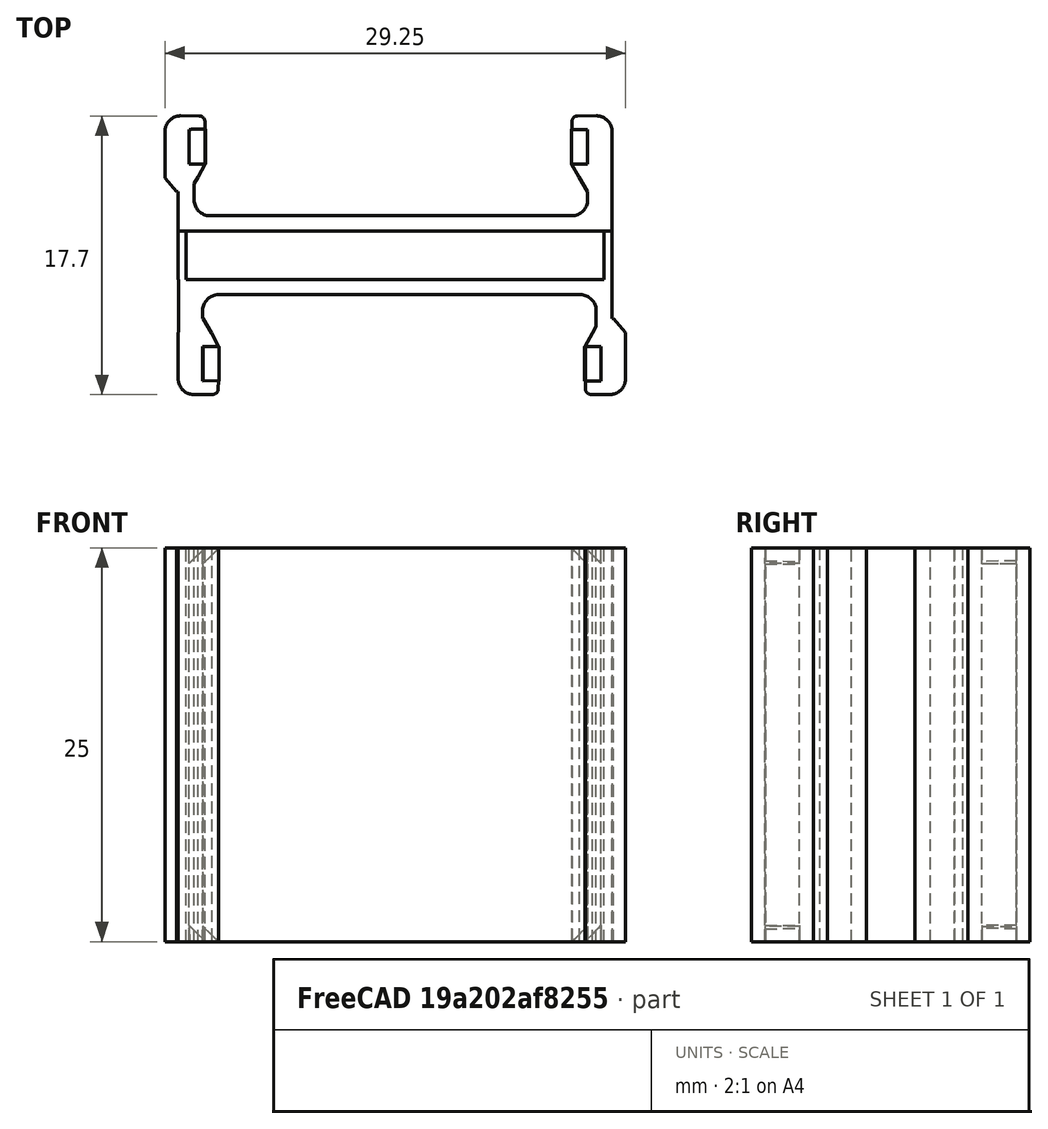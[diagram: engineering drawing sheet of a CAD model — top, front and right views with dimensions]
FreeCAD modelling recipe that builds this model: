
FCSTD DOCUMENT  (FreeCAD 0.18.4R)
Label: GSMBoardClip3
License: All rights reserved
LicenseURL: http://en.wikipedia.org/wiki/All_rights_reserved
objects: Sketcher::SketchObject×14, PartDesign::Pad×14, Part::MultiFuse×7, Part::Fillet×6, Part::Box×2, Mesh::Feature×1
note: 57 computed .brp shape members not serialized (recipe doc carries the construction recipe); baked Part::Feature solids carry a one-line shape summary decoded from their .brp

FEATURE [Sketcher::SketchObject] Sketch
  MapMode = 5
  sketch-geometry (8):
    g0: LineSegment StartX=-13.9908 StartY=-4.48975 StartZ=0 EndX=10.9903 EndY=-4.48975 EndZ=0
    g1: LineSegment StartX=12.5295 StartY=-5.45766 StartZ=0 EndX=-15.0007 EndY=-5.45766 EndZ=0
    g2: LineSegment StartX=-15.0007 StartY=-1.98555 StartZ=0 EndX=-13.9908 EndY=-1.98555 EndZ=0
    g3: LineSegment StartX=-13.9908 StartY=-1.98555 StartZ=0 EndX=-13.9908 EndY=-4.48975 EndZ=0
    g4: LineSegment StartX=-15.0007 StartY=-5.45766 StartZ=0 EndX=-15.0007 EndY=-1.98555 EndZ=0
    g5: LineSegment StartX=10.9903 StartY=-4.48975 StartZ=0 EndX=11.0098 EndY=-1.99154 EndZ=0
    g6: LineSegment StartX=11.0098 StartY=-1.99154 StartZ=0 EndX=12.5373 EndY=-1.98538 EndZ=0
    g7: LineSegment StartX=12.5373 StartY=-1.98538 StartZ=0 EndX=12.5295 EndY=-5.45766 EndZ=0
  constraints (13):
    c: Horizontal(g0)
    c: Horizontal(g1)
    c: Coincident(g2,g3)
    c: Coincident(g4,g2)
    c: Horizontal(g2)
    c: Vertical(g3)
    c: Vertical(g4)
    c: Coincident(g0,g3)
    c: Coincident(g4,g1)
    c: Coincident(g1,g7)
    c: Coincident(g0,g5)
    c: Coincident(g5,g6)
    c: Coincident(g6,g7)
FEATURE [Sketcher::SketchObject] Sketch004
  MapMode = 5
  Placement = pos=(-7.3,1,6.03) rot=(1,0,0;1.5708rad)
  sketch-geometry (3):
    g0: LineSegment StartX=-7.00166 StartY=-5.01077 StartZ=0 EndX=-6.98953 EndY=-6.02972 EndZ=0
    g1: LineSegment StartX=-6.98953 StartY=-6.02972 StartZ=0 EndX=-5.96627 EndY=-6.02972 EndZ=0
    g2: LineSegment StartX=-7.00166 StartY=-5.01077 StartZ=0 EndX=-5.96627 EndY=-6.02972 EndZ=0
  constraints (3):
    c: Coincident(g0,g1)
    c: Coincident(g2,g0)
    c: Coincident(g2,g1)
FEATURE [PartDesign::Pad] Pad004  label="stopper002"
  Length = 2.2
  Length2 = 100
  Placement = pos=(-7.3,1,6.03) rot=(1,0,0;1.5708rad)
  Profile = -> Sketch004
  Type = 0
FEATURE [Sketcher::SketchObject] Sketch008
  MapMode = 5
  Placement = pos=(-13.3,1,24.03) rot=(1,0,0;1.5708rad)
  sketch-geometry (3):
    g0: LineSegment StartX=-0.005347 StartY=0.971544 StartZ=0 EndX=-1.00207 EndY=-0.002707 EndZ=0
    g1: LineSegment StartX=-1.00207 StartY=-0.002707 StartZ=0 EndX=-1.00779 EndY=0.969763 EndZ=0
    g2: LineSegment StartX=-1.00779 StartY=0.969763 StartZ=0 EndX=-0.005347 EndY=0.971544 EndZ=0
  constraints (3):
    c: Coincident(g0,g1)
    c: Coincident(g1,g2)
    c: Coincident(g2,g0)
FEATURE [PartDesign::Pad] Pad008  label="stopper001"
  Length = 2.2
  Length2 = 100
  Placement = pos=(-13.3,1,24.03) rot=(1,0,0;1.5708rad)
  Profile = -> Sketch008
  Type = 0
FEATURE [Sketcher::SketchObject] Sketch009
  MapMode = 5
  Placement = pos=(-5.3,1,0) rot=(0,0,1;0rad)
  sketch-geometry (11):
    g0: LineSegment StartX=-10.5532 StartY=0.855362 StartZ=0 EndX=-8.36858 EndY=0.849458 EndZ=0
    g1: LineSegment StartX=-8.00975 StartY=0.49381 StartZ=0 EndX=-8.00369 EndY=-0.0300228 EndZ=0
    g2: LineSegment StartX=-8.00369 StartY=-0.0300228 StartZ=0 EndX=-8.99915 EndY=-0.016209 EndZ=0
    g3: LineSegment StartX=-8.99915 StartY=-0.016209 StartZ=0 EndX=-8.99963 EndY=-2.20954 EndZ=0
    g4: LineSegment StartX=-8.99963 StartY=-2.20954 StartZ=0 EndX=-7.98693 EndY=-2.20954 EndZ=0
    g5: LineSegment StartX=-7.98693 StartY=-2.20954 StartZ=0 EndX=-8.44936 EndY=-3.04943 EndZ=0
    g6: LineSegment StartX=-8.44936 StartY=-3.04943 StartZ=0 EndX=-8.98872 EndY=-3.96758 EndZ=0
    g7: LineSegment StartX=-8.98872 StartY=-3.96758 StartZ=0 EndX=-9.79483 EndY=-3.96363 EndZ=0
    g8: LineSegment StartX=-9.79483 StartY=-3.96363 StartZ=0 EndX=-10.5532 EndY=-3.09064 EndZ=0
    g9: LineSegment StartX=-10.5532 StartY=-3.09064 StartZ=0 EndX=-10.5532 EndY=0.855362 EndZ=0
    g10: ArcOfCircle CenterX=-8.36955 CenterY=0.489641 CenterZ=0 NormalX=0 NormalY=0 NormalZ=1 AngleXU=0 Radius=0.359818 StartAngle=0.0115851 EndAngle=1.56809
  constraints (11):
    c: Coincident(g1,g2)
    c: Coincident(g2,g3)
    c: Coincident(g3,g4)
    c: Coincident(g4,g5)
    c: Coincident(g5,g6)
    c: Coincident(g6,g7)
    c: Tangent(g0,g10) = 1.5708
    c: Tangent(g1,g10) = 1.5708
    c: Coincident(g9,g0)
    c: Coincident(g9,g8)
    c: Coincident(g8,g7)
FEATURE [PartDesign::Pad] Pad009  label="Snap001"
  Length = 25
  Length2 = 100
  Placement = pos=(-5.3,1,0) rot=(0,0,1;0rad)
  Profile = -> Sketch009
  Type = 0
FEATURE [Part::MultiFuse] Fusion  label="SnapLeft"
  Shapes = -> [Pad009,Pad008,Pad004]
FEATURE [Sketcher::SketchObject] Sketch010
  MapMode = 5
  Placement = pos=(-7.3,1,6.03) rot=(1,0,0;1.5708rad)
  sketch-geometry (3):
    g0: LineSegment StartX=-7.00166 StartY=-5.01077 StartZ=0 EndX=-6.98953 EndY=-6.02972 EndZ=0
    g1: LineSegment StartX=-6.98953 StartY=-6.02972 StartZ=0 EndX=-5.96627 EndY=-6.02972 EndZ=0
    g2: LineSegment StartX=-7.00166 StartY=-5.01077 StartZ=0 EndX=-5.96627 EndY=-6.02972 EndZ=0
  constraints (3):
    c: Coincident(g0,g1)
    c: Coincident(g2,g0)
    c: Coincident(g2,g1)
FEATURE [PartDesign::Pad] Pad010  label="stopper003"
  Length = 2.2
  Length2 = 100
  Placement = pos=(-7.3,1,6.03) rot=(1,0,0;1.5708rad)
  Profile = -> Sketch010
  Type = 0
FEATURE [Sketcher::SketchObject] Sketch011
  MapMode = 5
  Placement = pos=(-13.3,1,24.03) rot=(1,0,0;1.5708rad)
  sketch-geometry (3):
    g0: LineSegment StartX=-0.005347 StartY=0.971544 StartZ=0 EndX=-1.00207 EndY=-0.002707 EndZ=0
    g1: LineSegment StartX=-1.00207 StartY=-0.002707 StartZ=0 EndX=-1.00779 EndY=0.969763 EndZ=0
    g2: LineSegment StartX=-1.00779 StartY=0.969763 StartZ=0 EndX=-0.005347 EndY=0.971544 EndZ=0
  constraints (3):
    c: Coincident(g0,g1)
    c: Coincident(g1,g2)
    c: Coincident(g2,g0)
FEATURE [PartDesign::Pad] Pad011  label="stopper004"
  Length = 2.2
  Length2 = 100
  Placement = pos=(-13.3,1,24.03) rot=(1,0,0;1.5708rad)
  Profile = -> Sketch011
  Type = 0
FEATURE [Sketcher::SketchObject] Sketch012
  MapMode = 5
  Placement = pos=(-5.3,1,0) rot=(0,0,1;0rad)
  sketch-geometry (11):
    g0: LineSegment StartX=-10.5532 StartY=0.855362 StartZ=0 EndX=-8.36858 EndY=0.849458 EndZ=0
    g1: LineSegment StartX=-8.00975 StartY=0.49381 StartZ=0 EndX=-8.00369 EndY=-0.0300228 EndZ=0
    g2: LineSegment StartX=-8.00369 StartY=-0.0300228 StartZ=0 EndX=-8.99915 EndY=-0.016209 EndZ=0
    g3: LineSegment StartX=-8.99915 StartY=-0.016209 StartZ=0 EndX=-8.99963 EndY=-2.20954 EndZ=0
    g4: LineSegment StartX=-8.99963 StartY=-2.20954 StartZ=0 EndX=-7.98693 EndY=-2.20954 EndZ=0
    g5: LineSegment StartX=-7.98693 StartY=-2.20954 StartZ=0 EndX=-8.44936 EndY=-3.04943 EndZ=0
    g6: LineSegment StartX=-8.44936 StartY=-3.04943 StartZ=0 EndX=-8.98872 EndY=-3.96758 EndZ=0
    g7: LineSegment StartX=-8.98872 StartY=-3.96758 StartZ=0 EndX=-9.79483 EndY=-3.96363 EndZ=0
    g8: LineSegment StartX=-9.79483 StartY=-3.96363 StartZ=0 EndX=-10.5532 EndY=-3.09064 EndZ=0
    g9: LineSegment StartX=-10.5532 StartY=-3.09064 StartZ=0 EndX=-10.5532 EndY=0.855362 EndZ=0
    g10: ArcOfCircle CenterX=-8.36955 CenterY=0.489641 CenterZ=0 NormalX=0 NormalY=0 NormalZ=1 AngleXU=0 Radius=0.359818 StartAngle=0.0115851 EndAngle=1.56809
  constraints (11):
    c: Coincident(g1,g2)
    c: Coincident(g2,g3)
    c: Coincident(g3,g4)
    c: Coincident(g4,g5)
    c: Coincident(g5,g6)
    c: Coincident(g6,g7)
    c: Tangent(g0,g10) = 1.5708
    c: Tangent(g1,g10) = 1.5708
    c: Coincident(g9,g0)
    c: Coincident(g9,g8)
    c: Coincident(g8,g7)
FEATURE [PartDesign::Pad] Pad012  label="Snap002"
  Length = 25
  Length2 = 100
  Placement = pos=(-5.3,1,0) rot=(0,0,1;0rad)
  Profile = -> Sketch012
  Type = 0
FEATURE [Part::MultiFuse] Fusion001  label="SnapRight"
  Placement = pos=(-3.3,0,25) rot=(0,1,0;3.14159rad)
  Shapes = -> [Pad012,Pad011,Pad010]
FEATURE [PartDesign::Pad] Pad
  Length = 25
  Length2 = 100
  Profile = -> Sketch
  Type = 0
FEATURE [Part::Fillet] Fillet
  Base = -> Pad
  Edges = 2 edges r=1: [Edge1,Edge2]
FEATURE [Part::Fillet] Fillet001
  Base = -> Fusion
  Edges = 1 edges r=1: [Edge59]
FEATURE [Part::Fillet] Fillet002
  Base = -> Fusion001
  Edges = 1 edges r=1: [Edge59]
FEATURE [Part::MultiFuse] Fusion002  label="GSMClip3_001"
  Shapes = -> [Fillet,Fillet001,Fillet002]
FEATURE [Sketcher::SketchObject] Sketch013
  MapMode = 5
  sketch-geometry (8):
    g0: LineSegment StartX=-13.9908 StartY=-4.48975 StartZ=0 EndX=10.9903 EndY=-4.48975 EndZ=0
    g1: LineSegment StartX=12.5295 StartY=-5.45766 StartZ=0 EndX=-15.0007 EndY=-5.45766 EndZ=0
    g2: LineSegment StartX=-15.0007 StartY=-1.98555 StartZ=0 EndX=-13.9908 EndY=-1.98555 EndZ=0
    g3: LineSegment StartX=-13.9908 StartY=-1.98555 StartZ=0 EndX=-13.9908 EndY=-4.48975 EndZ=0
    g4: LineSegment StartX=-15.0007 StartY=-5.45766 StartZ=0 EndX=-15.0007 EndY=-1.98555 EndZ=0
    g5: LineSegment StartX=10.9903 StartY=-4.48975 StartZ=0 EndX=11.0098 EndY=-1.99154 EndZ=0
    g6: LineSegment StartX=11.0098 StartY=-1.99154 StartZ=0 EndX=12.5373 EndY=-1.98538 EndZ=0
    g7: LineSegment StartX=12.5373 StartY=-1.98538 StartZ=0 EndX=12.5295 EndY=-5.45766 EndZ=0
  constraints (13):
    c: Horizontal(g0)
    c: Horizontal(g1)
    c: Coincident(g2,g3)
    c: Coincident(g4,g2)
    c: Horizontal(g2)
    c: Vertical(g3)
    c: Vertical(g4)
    c: Coincident(g0,g3)
    c: Coincident(g4,g1)
    c: Coincident(g1,g7)
    c: Coincident(g0,g5)
    c: Coincident(g5,g6)
    c: Coincident(g6,g7)
FEATURE [PartDesign::Pad] Pad013
  Length = 25
  Length2 = 100
  Profile = -> Sketch013
  Type = 0
FEATURE [Part::Fillet] Fillet003
  Base = -> Pad013
  Edges = 2 edges r=1: [Edge1,Edge2]
FEATURE [Sketcher::SketchObject] Sketch014
  MapMode = 5
  Placement = pos=(-7.3,1,6.03) rot=(1,0,0;1.5708rad)
  sketch-geometry (3):
    g0: LineSegment StartX=-7.00166 StartY=-5.01077 StartZ=0 EndX=-6.98953 EndY=-6.02972 EndZ=0
    g1: LineSegment StartX=-6.98953 StartY=-6.02972 StartZ=0 EndX=-5.96627 EndY=-6.02972 EndZ=0
    g2: LineSegment StartX=-7.00166 StartY=-5.01077 StartZ=0 EndX=-5.96627 EndY=-6.02972 EndZ=0
  constraints (3):
    c: Coincident(g0,g1)
    c: Coincident(g2,g0)
    c: Coincident(g2,g1)
FEATURE [PartDesign::Pad] Pad014  label="stopper005"
  Length = 2.2
  Length2 = 100
  Placement = pos=(-7.3,1,6.03) rot=(1,0,0;1.5708rad)
  Profile = -> Sketch014
  Type = 0
FEATURE [Sketcher::SketchObject] Sketch015
  MapMode = 5
  Placement = pos=(-13.3,1,24.03) rot=(1,0,0;1.5708rad)
  sketch-geometry (3):
    g0: LineSegment StartX=-0.005347 StartY=0.971544 StartZ=0 EndX=-1.00207 EndY=-0.002707 EndZ=0
    g1: LineSegment StartX=-1.00207 StartY=-0.002707 StartZ=0 EndX=-1.00779 EndY=0.969763 EndZ=0
    g2: LineSegment StartX=-1.00779 StartY=0.969763 StartZ=0 EndX=-0.005347 EndY=0.971544 EndZ=0
  constraints (3):
    c: Coincident(g0,g1)
    c: Coincident(g1,g2)
    c: Coincident(g2,g0)
FEATURE [PartDesign::Pad] Pad015  label="stopper006"
  Length = 2.2
  Length2 = 100
  Placement = pos=(-13.3,1,24.03) rot=(1,0,0;1.5708rad)
  Profile = -> Sketch015
  Type = 0
FEATURE [Sketcher::SketchObject] Sketch016
  MapMode = 5
  Placement = pos=(-13.3,1,24.03) rot=(1,0,0;1.5708rad)
  sketch-geometry (3):
    g0: LineSegment StartX=-0.005347 StartY=0.971544 StartZ=0 EndX=-1.00207 EndY=-0.002707 EndZ=0
    g1: LineSegment StartX=-1.00207 StartY=-0.002707 StartZ=0 EndX=-1.00779 EndY=0.969763 EndZ=0
    g2: LineSegment StartX=-1.00779 StartY=0.969763 StartZ=0 EndX=-0.005347 EndY=0.971544 EndZ=0
  constraints (3):
    c: Coincident(g0,g1)
    c: Coincident(g1,g2)
    c: Coincident(g2,g0)
FEATURE [PartDesign::Pad] Pad017  label="stopper007"
  Length = 2.2
  Length2 = 100
  Placement = pos=(-13.3,1,24.03) rot=(1,0,0;1.5708rad)
  Profile = -> Sketch016
  Type = 0
FEATURE [Sketcher::SketchObject] Sketch017
  MapMode = 5
  Placement = pos=(-5.3,1,0) rot=(0,0,1;0rad)
  sketch-geometry (11):
    g0: LineSegment StartX=-10.5532 StartY=0.855362 StartZ=0 EndX=-8.36858 EndY=0.849458 EndZ=0
    g1: LineSegment StartX=-8.00975 StartY=0.49381 StartZ=0 EndX=-8.00369 EndY=-0.0300228 EndZ=0
    g2: LineSegment StartX=-8.00369 StartY=-0.0300228 StartZ=0 EndX=-8.99915 EndY=-0.016209 EndZ=0
    g3: LineSegment StartX=-8.99915 StartY=-0.016209 StartZ=0 EndX=-8.99963 EndY=-2.20954 EndZ=0
    g4: LineSegment StartX=-8.99963 StartY=-2.20954 StartZ=0 EndX=-7.98693 EndY=-2.20954 EndZ=0
    g5: LineSegment StartX=-7.98693 StartY=-2.20954 StartZ=0 EndX=-8.44936 EndY=-3.04943 EndZ=0
    g6: LineSegment StartX=-8.44936 StartY=-3.04943 StartZ=0 EndX=-8.98872 EndY=-3.96758 EndZ=0
    g7: LineSegment StartX=-8.98872 StartY=-3.96758 StartZ=0 EndX=-9.79483 EndY=-3.96363 EndZ=0
    g8: LineSegment StartX=-9.79483 StartY=-3.96363 StartZ=0 EndX=-10.5532 EndY=-3.09064 EndZ=0
    g9: LineSegment StartX=-10.5532 StartY=-3.09064 StartZ=0 EndX=-10.5532 EndY=0.855362 EndZ=0
    g10: ArcOfCircle CenterX=-8.36955 CenterY=0.489641 CenterZ=0 NormalX=0 NormalY=0 NormalZ=1 AngleXU=0 Radius=0.359818 StartAngle=0.0115851 EndAngle=1.56809
  constraints (11):
    c: Coincident(g1,g2)
    c: Coincident(g2,g3)
    c: Coincident(g3,g4)
    c: Coincident(g4,g5)
    c: Coincident(g5,g6)
    c: Coincident(g6,g7)
    c: Tangent(g0,g10) = 1.5708
    c: Tangent(g1,g10) = 1.5708
    c: Coincident(g9,g0)
    c: Coincident(g9,g8)
    c: Coincident(g8,g7)
FEATURE [PartDesign::Pad] Pad018  label="Snap004"
  Length = 25
  Length2 = 100
  Placement = pos=(-5.3,1,0) rot=(0,0,1;0rad)
  Profile = -> Sketch017
  Type = 0
FEATURE [Sketcher::SketchObject] Sketch018
  MapMode = 5
  Placement = pos=(-7.3,1,6.03) rot=(1,0,0;1.5708rad)
  sketch-geometry (3):
    g0: LineSegment StartX=-7.00166 StartY=-5.01077 StartZ=0 EndX=-6.98953 EndY=-6.02972 EndZ=0
    g1: LineSegment StartX=-6.98953 StartY=-6.02972 StartZ=0 EndX=-5.96627 EndY=-6.02972 EndZ=0
    g2: LineSegment StartX=-7.00166 StartY=-5.01077 StartZ=0 EndX=-5.96627 EndY=-6.02972 EndZ=0
  constraints (3):
    c: Coincident(g0,g1)
    c: Coincident(g2,g0)
    c: Coincident(g2,g1)
FEATURE [PartDesign::Pad] Pad019  label="stopper008"
  Length = 2.2
  Length2 = 100
  Placement = pos=(-7.3,1,6.03) rot=(1,0,0;1.5708rad)
  Profile = -> Sketch018
  Type = 0
FEATURE [Part::MultiFuse] Fusion003  label="SnapRight001"
  Placement = pos=(-3.3,0,25) rot=(0,1,0;3.14159rad)
  Shapes = -> [Pad018,Pad017,Pad019]
FEATURE [Sketcher::SketchObject] Sketch019
  MapMode = 5
  Placement = pos=(-5.3,1,0) rot=(0,0,1;0rad)
  sketch-geometry (11):
    g0: LineSegment StartX=-10.5532 StartY=0.855362 StartZ=0 EndX=-8.36858 EndY=0.849458 EndZ=0
    g1: LineSegment StartX=-8.00975 StartY=0.49381 StartZ=0 EndX=-8.00369 EndY=-0.0300228 EndZ=0
    g2: LineSegment StartX=-8.00369 StartY=-0.0300228 StartZ=0 EndX=-8.99915 EndY=-0.016209 EndZ=0
    g3: LineSegment StartX=-8.99915 StartY=-0.016209 StartZ=0 EndX=-8.99963 EndY=-2.20954 EndZ=0
    g4: LineSegment StartX=-8.99963 StartY=-2.20954 StartZ=0 EndX=-7.98693 EndY=-2.20954 EndZ=0
    g5: LineSegment StartX=-7.98693 StartY=-2.20954 StartZ=0 EndX=-8.44936 EndY=-3.04943 EndZ=0
    g6: LineSegment StartX=-8.44936 StartY=-3.04943 StartZ=0 EndX=-8.98872 EndY=-3.96758 EndZ=0
    g7: LineSegment StartX=-8.98872 StartY=-3.96758 StartZ=0 EndX=-9.79483 EndY=-3.96363 EndZ=0
    g8: LineSegment StartX=-9.79483 StartY=-3.96363 StartZ=0 EndX=-10.5532 EndY=-3.09064 EndZ=0
    g9: LineSegment StartX=-10.5532 StartY=-3.09064 StartZ=0 EndX=-10.5532 EndY=0.855362 EndZ=0
    g10: ArcOfCircle CenterX=-8.36955 CenterY=0.489641 CenterZ=0 NormalX=0 NormalY=0 NormalZ=1 AngleXU=0 Radius=0.359818 StartAngle=0.0115851 EndAngle=1.56809
  constraints (11):
    c: Coincident(g1,g2)
    c: Coincident(g2,g3)
    c: Coincident(g3,g4)
    c: Coincident(g4,g5)
    c: Coincident(g5,g6)
    c: Coincident(g6,g7)
    c: Tangent(g0,g10) = 1.5708
    c: Tangent(g1,g10) = 1.5708
    c: Coincident(g9,g0)
    c: Coincident(g9,g8)
    c: Coincident(g8,g7)
FEATURE [PartDesign::Pad] Pad016  label="Snap003"
  Length = 25
  Length2 = 100
  Placement = pos=(-5.3,1,0) rot=(0,0,1;0rad)
  Profile = -> Sketch019
  Type = 0
FEATURE [Part::MultiFuse] Fusion005  label="SnapLeft001"
  Shapes = -> [Pad016,Pad015,Pad014]
FEATURE [Part::Fillet] Fillet004
  Base = -> Fusion003
  Edges = 1 edges r=1: [Edge59]
FEATURE [Part::Fillet] Fillet005
  Base = -> Fusion005
  Edges = 1 edges r=1: [Edge59]
FEATURE [Part::MultiFuse] Fusion004  label="GSMClip3_002"
  Placement = pos=(-2.45,-14,0) rot=(0,0,1;3.14159rad)
  Shapes = -> [Fillet003,Fillet005,Fillet004]
FEATURE [Part::Box] Box002  label="Würfel002"
  AttacherType = Attacher::AttachEngine3D
  Height = 25
  Length = 0.5
  Placement = pos=(12.05,-8.56,0) rot=(0,0,1;0rad)
  Width = 3.1
FEATURE [Part::Box] Box003  label="Würfel003"
  AttacherType = Attacher::AttachEngine3D
  Height = 25
  Length = 0.5
  Placement = pos=(-15,-8.56,0) rot=(0,0,1;0rad)
  Width = 3.1
FEATURE [Part::MultiFuse] Fusion006
  Shapes = -> [Box002,Fusion002,Box003,Fusion004]
FEATURE [Mesh::Feature] Mesh  label="Fusion006 (Meshed)"
